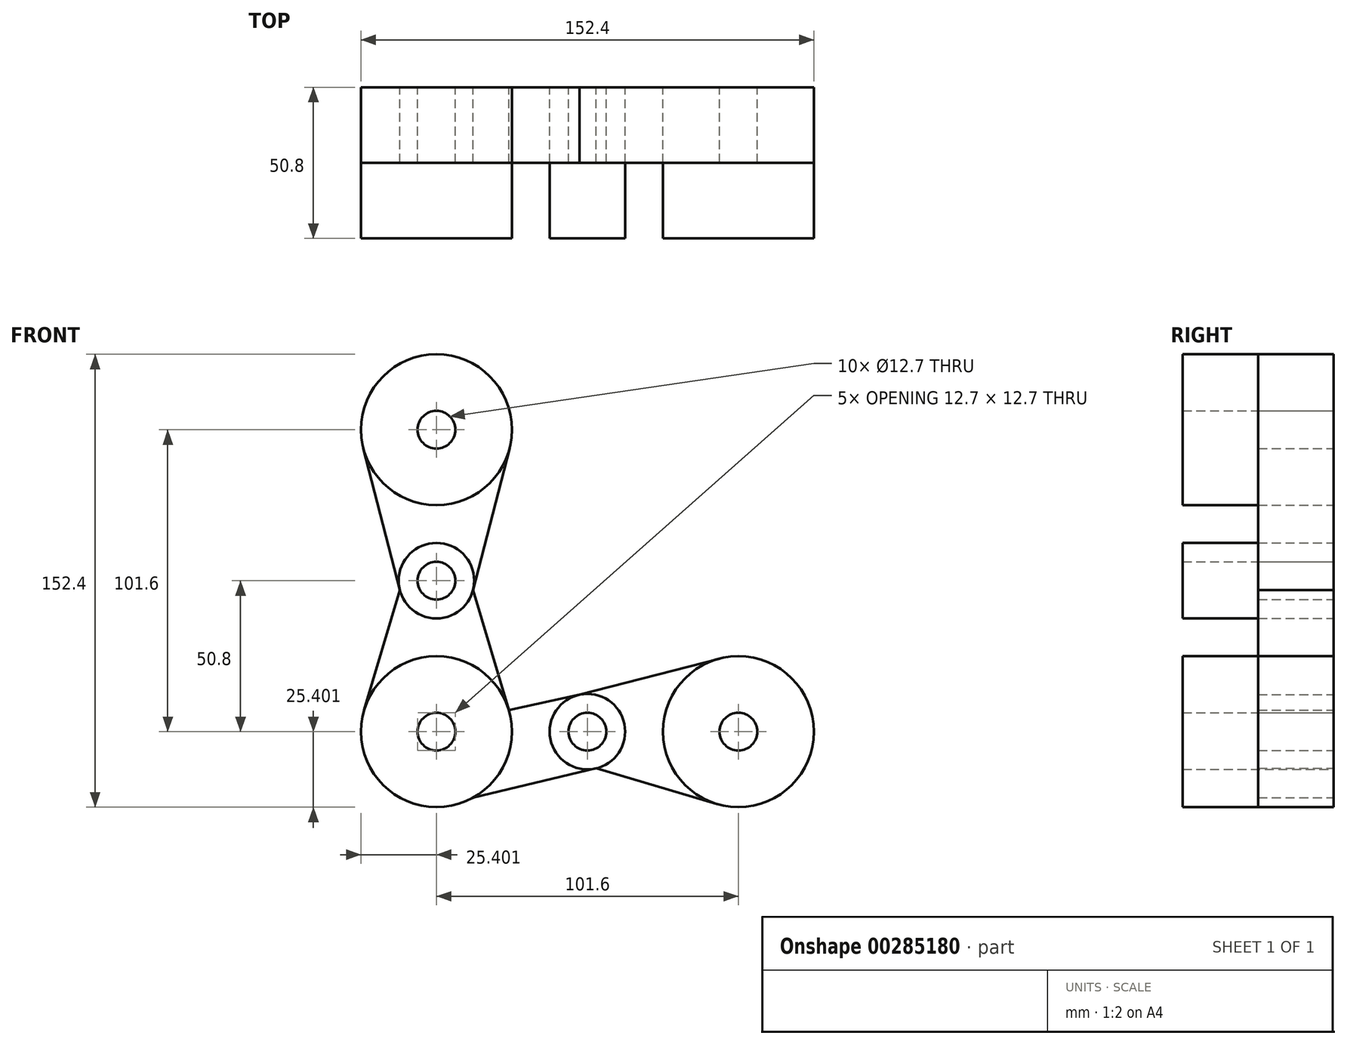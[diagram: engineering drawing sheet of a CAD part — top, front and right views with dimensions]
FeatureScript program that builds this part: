
annotation { "Feature Type Name" : "Feature", "Feature Type Description" : "" }
export const myFeature = defineFeature(function(context is Context, id is Id, definition is map)
    precondition{}
    {
        {
            var Q0;
            Q0=qCreatedBy(makeId("Front.planeOp"),FACE);
            var sketch = newSketch(context, id + "F0", { "sketchPlane" : qUnion([Q0])});
            skLineSegment(sketch, "E0", {"start": v(-76.69, -76.45) * mm, "end": v(-25.89, -76.45) * mm});
            skLineSegment(sketch, "E1", {"start": v(-25.89, -76.45) * mm, "end": v(24.91, -76.45) * mm});
            skLineSegment(sketch, "E2", {"start": v(-76.69, -76.45) * mm, "end": v(-76.69, -25.65) * mm});
            skLineSegment(sketch, "E3", {"start": v(-76.69, -25.65) * mm, "end": v(-76.69, 25.15) * mm});
            skCircle(sketch, "E4", {"center": v(-76.69, 25.15) * mm, "radius": 25.4 * mm});
            skCircle(sketch, "E5", {"center": v(-76.69, -76.45) * mm, "radius": 25.4 * mm});
            skCircle(sketch, "E6", {"center": v(24.91, -76.45) * mm, "radius": 25.4 * mm});
            skCircle(sketch, "E7", {"center": v(-76.69, -25.65) * mm, "radius": 12.7 * mm});
            skCircle(sketch, "E8", {"center": v(-25.89, -76.45) * mm, "radius": 12.7 * mm});
            skLineSegment(sketch, "E9", {"start": v(-101.28, 18.8) * mm, "end": v(-88.99, -28.82) * mm});
            skLineSegment(sketch, "E10", {"start": v(-52.1, 18.8) * mm, "end": v(-64.4, -28.82) * mm});
            skLineSegment(sketch, "E11", {"start": v(-88.99, -28.82) * mm, "end": v(-101.03, -69.19) * mm});
            skLineSegment(sketch, "E12", {"start": v(-64.4, -28.82) * mm, "end": v(-52.35, -69.19) * mm});
            skLineSegment(sketch, "E13", {"start": v(-52.35, -69.19) * mm, "end": v(-28.58, -64.04) * mm});
            skLineSegment(sketch, "E14", {"start": v(-64.4, -98.67) * mm, "end": v(-22.95, -88.8) * mm});
            skLineSegment(sketch, "E15", {"start": v(-28.58, -64.04) * mm, "end": v(18.56, -51.86) * mm});
            skLineSegment(sketch, "E16", {"start": v(-22.95, -88.8) * mm, "end": v(18.56, -101.06) * mm});
            skSolve(sketch);
        }
        {
            var Q0;
            {var subQ0=sQuery(id+"F0.wireOp",EDGE,"E4");var subQ1=makeQuery(id+"F0.imprint","INTERSECT",VERTEX,{"derivedFrom":[subQ0,sQuery(id+"F0.wireOp",EDGE,"E9")]});Q0=makeQuery(id+"F0.imprint","IMPRINT",FACE,{"disambiguationData":[TD([[makeQuery(id+"F0.imprint","IMPRINT",EDGE,{"disambiguationData":[TD([[subQ1,-1.0]])],"derivedFrom":subQ0}),1.0]])]});}
            var Q1;
            {var subQ0=sQuery(id+"F0.wireOp",EDGE,"E6");var subQ1=makeQuery(id+"F0.imprint","INTERSECT",VERTEX,{"derivedFrom":[subQ0,sQuery(id+"F0.wireOp",EDGE,"E15")]});Q1=makeQuery(id+"F0.imprint","IMPRINT",FACE,{"disambiguationData":[TD([[makeQuery(id+"F0.imprint","IMPRINT",EDGE,{"disambiguationData":[TD([[subQ1,-1.0]])],"derivedFrom":subQ0}),1.0]])]});}
            var Q2;
            {var subQ0=sQuery(id+"F0.wireOp",EDGE,"E3");var subQ1=sQuery(id+"F0.wireOp",EDGE,"E2");var subQ2=makeQuery(id+"F0.imprint","INTERSECT",VERTEX,{"derivedFrom":[subQ1,subQ0]});Q2=makeQuery(id+"F0.imprint","IMPRINT",FACE,{"disambiguationData":[TD([[makeQuery(id+"F0.imprint","IMPRINT",EDGE,{"disambiguationData":[TD([[subQ2,1.0]])],"derivedFrom":subQ1}),1.0]])]});}
            var Q3;
            {var subQ0=sQuery(id+"F0.wireOp",EDGE,"E3");var subQ1=sQuery(id+"F0.wireOp",EDGE,"E2");var subQ2=makeQuery(id+"F0.imprint","INTERSECT",VERTEX,{"derivedFrom":[subQ1,subQ0]});Q3=makeQuery(id+"F0.imprint","IMPRINT",FACE,{"disambiguationData":[TD([[makeQuery(id+"F0.imprint","IMPRINT",EDGE,{"disambiguationData":[TD([[subQ2,1.0]])],"derivedFrom":subQ1}),-1.0]])]});}
            var Q4;
            {var subQ3=sQuery(id+"F0.wireOp",EDGE,"E2");var subQ4=sQuery(id+"F0.wireOp",EDGE,"E0");var subQ5=makeQuery(id+"F0.imprint","INTERSECT",VERTEX,{"derivedFrom":[subQ4,subQ3]});Q4=makeQuery(id+"F0.imprint","IMPRINT",FACE,{"disambiguationData":[TD([[makeQuery(id+"F0.imprint","IMPRINT",EDGE,{"disambiguationData":[TD([[subQ5,-1.0]])],"derivedFrom":subQ4}),-1.0]])]});}
            var Q5;
            {var subQ0=sQuery(id+"F0.wireOp",EDGE,"E2");var subQ1=sQuery(id+"F0.wireOp",EDGE,"E0");var subQ2=makeQuery(id+"F0.imprint","INTERSECT",VERTEX,{"derivedFrom":[subQ1,subQ0]});Q5=makeQuery(id+"F0.imprint","IMPRINT",FACE,{"disambiguationData":[TD([[makeQuery(id+"F0.imprint","IMPRINT",EDGE,{"disambiguationData":[TD([[subQ2,-1.0]])],"derivedFrom":subQ1}),1.0]])]});}
            var Q6;
            {var subQ0=sQuery(id+"F0.wireOp",EDGE,"E1");var subQ1=sQuery(id+"F0.wireOp",EDGE,"E0");var subQ2=makeQuery(id+"F0.imprint","INTERSECT",VERTEX,{"derivedFrom":[subQ1,subQ0]});Q6=makeQuery(id+"F0.imprint","IMPRINT",FACE,{"disambiguationData":[TD([[makeQuery(id+"F0.imprint","IMPRINT",EDGE,{"disambiguationData":[TD([[subQ2,1.0]])],"derivedFrom":subQ1}),1.0]])]});}
            var Q7;
            {var subQ0=sQuery(id+"F0.wireOp",EDGE,"E1");var subQ1=sQuery(id+"F0.wireOp",EDGE,"E0");var subQ2=makeQuery(id+"F0.imprint","INTERSECT",VERTEX,{"derivedFrom":[subQ1,subQ0]});Q7=makeQuery(id+"F0.imprint","IMPRINT",FACE,{"disambiguationData":[TD([[makeQuery(id+"F0.imprint","IMPRINT",EDGE,{"disambiguationData":[TD([[subQ2,1.0]])],"derivedFrom":subQ1}),-1.0]])]});}
            extrude(context, id + "F1", {"entities" : qUnion([Q0, Q1, Q2, Q3, Q4, Q5, Q6, Q7]), "depth" : 50.8 * mm});
        }
        {
            var Q0;
            Q0 = qSketchRegion(id + "F0", true);
            extrude(context, id + "F2", {"entities" : qUnion([Q0]), "depth" : 25.4 * mm});
        }
        {
            var Q0;
            Q0=sQuery(id+"F0.wireOp",VERTEX,"E3.end");
            var Q1;
            Q1=sQuery(id+"F0.wireOp",VERTEX,"E7.center");
            var Q2;
            Q2=sQuery(id+"F0.wireOp",VERTEX,"E5.center");
            var Q3;
            Q3=sQuery(id+"F0.wireOp",VERTEX,"E1.start");
            var Q4;
            Q4=sQuery(id+"F0.wireOp",VERTEX,"E1.end");
            var Q5;
            Q5=makeQuery(id+"F1.opExtrude","SWEPT_BODY",BODY,{"disambiguationData":[OSD([sQuery(id+"F0.wireOp",EDGE,"E4")])]});
            var Q6;
            Q6=makeQuery(id+"F2.opExtrude","SWEPT_BODY",BODY,{"disambiguationData":[OSD([sQuery(id+"F0.wireOp",EDGE,"E4"),sQuery(id+"F0.wireOp",EDGE,"E5"),sQuery(id+"F0.wireOp",EDGE,"E6"),sQuery(id+"F0.wireOp",EDGE,"E9"),sQuery(id+"F0.wireOp",EDGE,"E10"),sQuery(id+"F0.wireOp",EDGE,"E11"),sQuery(id+"F0.wireOp",EDGE,"E12"),sQuery(id+"F0.wireOp",EDGE,"E13"),sQuery(id+"F0.wireOp",EDGE,"E14"),sQuery(id+"F0.wireOp",EDGE,"E15"),sQuery(id+"F0.wireOp",EDGE,"E16")])]});
            var Q7;
            Q7=makeQuery(id+"F1.opExtrude","SWEPT_BODY",BODY,{"disambiguationData":[OSD([sQuery(id+"F0.wireOp",EDGE,"E7")])]});
            var Q8;
            Q8=makeQuery(id+"F1.opExtrude","SWEPT_BODY",BODY,{"disambiguationData":[OSD([sQuery(id+"F0.wireOp",EDGE,"E5")])]});
            var Q9;
            Q9=makeQuery(id+"F1.opExtrude","SWEPT_BODY",BODY,{"disambiguationData":[OSD([sQuery(id+"F0.wireOp",EDGE,"E8")])]});
            var Q10;
            Q10=makeQuery(id+"F1.opExtrude","SWEPT_BODY",BODY,{"disambiguationData":[OSD([sQuery(id+"F0.wireOp",EDGE,"E6")])]});
            hole(context, id + "F3", {"style" : HoleStyle.SIMPLE, "endStyle" : HoleEndStyle.THROUGH, "oppositeDirection" : true, "holeDiameter" : 12.7 * mm, "tappedDepth" : 12.7 * mm, "tapClearance" : 3, "locations" : qUnion([Q0, Q1, Q2, Q3, Q4]), "scope" : qUnion([Q5, Q6, Q7, Q8, Q9, Q10])});
        }
    });
